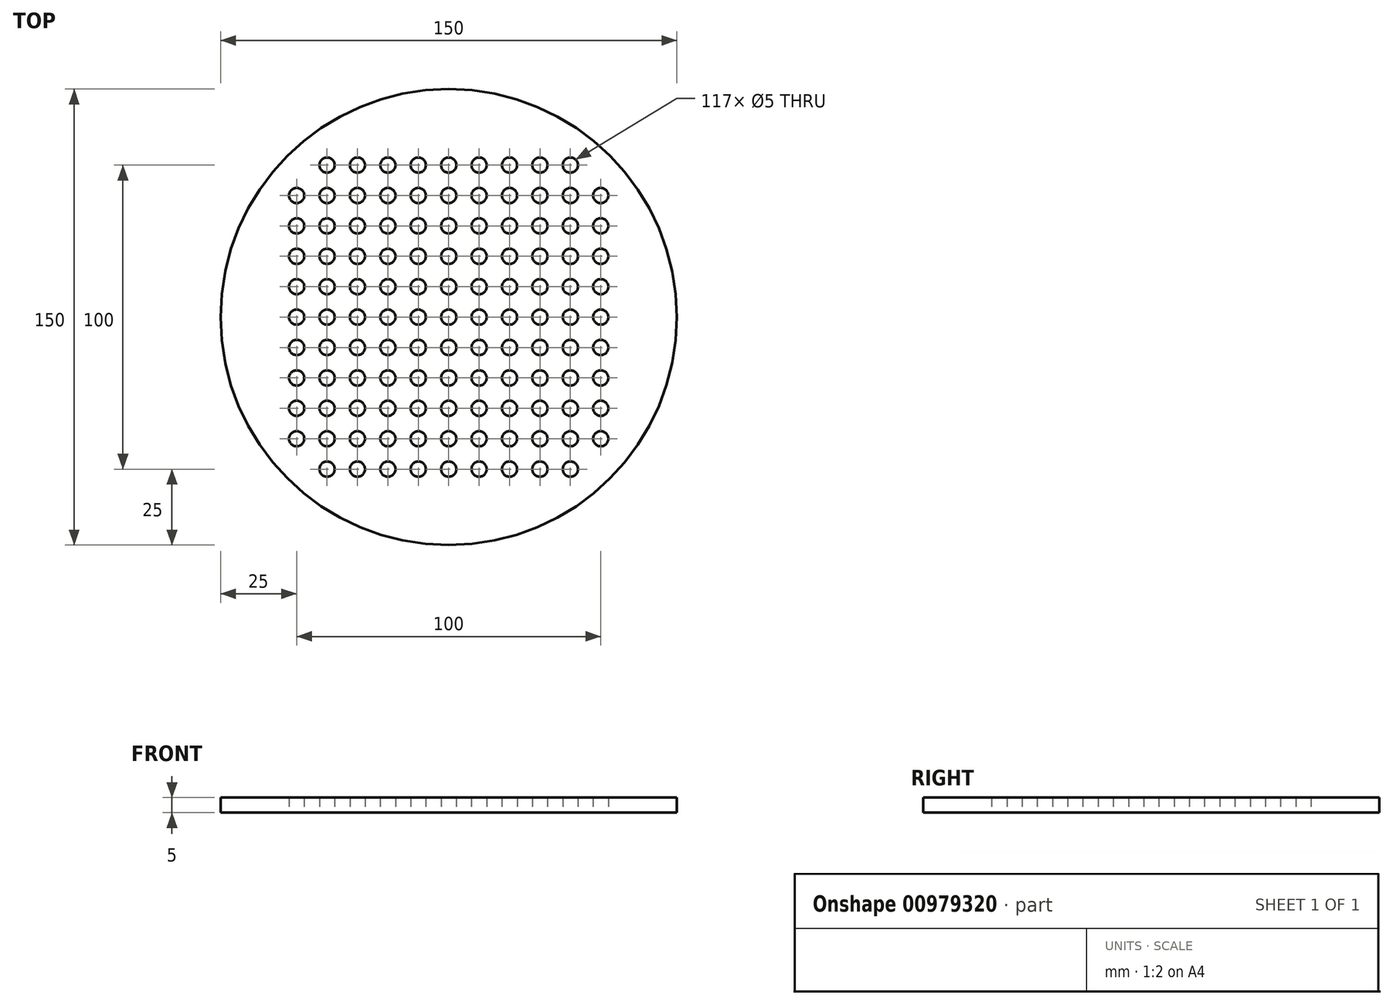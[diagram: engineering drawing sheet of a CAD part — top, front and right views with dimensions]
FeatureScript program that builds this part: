
annotation { "Feature Type Name" : "Feature", "Feature Type Description" : "" }
export const myFeature = defineFeature(function(context is Context, id is Id, definition is map)
    precondition{}
    {
        {
            var Q0;
            Q0=qCreatedBy(makeId("Top.planeOp"),FACE);
            var sketch = newSketch(context, id + "F0", { "sketchPlane" : qUnion([Q0])});
            skCircle(sketch, "E0", {"center": v(0, 0) * mm, "radius": 75 * mm});
            skCircle(sketch, "E1", {"center": v(0, 0) * mm, "radius": 2.5 * mm});
            skCircle(sketch, "E2.0.1.0", {"center": v(0, 10) * mm, "radius": 2.5 * mm});
            skCircle(sketch, "E2.0.2.0", {"center": v(0, 20) * mm, "radius": 2.5 * mm});
            skCircle(sketch, "E2.0.3.0", {"center": v(0, 30) * mm, "radius": 2.5 * mm});
            skCircle(sketch, "E2.0.4.0", {"center": v(0, 40) * mm, "radius": 2.5 * mm});
            skCircle(sketch, "E2.0.5.0", {"center": v(0, 50) * mm, "radius": 2.5 * mm});
            skCircle(sketch, "E2.1.0.0", {"center": v(10, 0) * mm, "radius": 2.5 * mm});
            skCircle(sketch, "E2.1.1.0", {"center": v(10, 10) * mm, "radius": 2.5 * mm});
            skCircle(sketch, "E2.1.2.0", {"center": v(10, 20) * mm, "radius": 2.5 * mm});
            skCircle(sketch, "E2.1.3.0", {"center": v(10, 30) * mm, "radius": 2.5 * mm});
            skCircle(sketch, "E2.1.4.0", {"center": v(10, 40) * mm, "radius": 2.5 * mm});
            skCircle(sketch, "E2.1.5.0", {"center": v(10, 50) * mm, "radius": 2.5 * mm});
            skCircle(sketch, "E2.2.0.0", {"center": v(20, 0) * mm, "radius": 2.5 * mm});
            skCircle(sketch, "E2.2.1.0", {"center": v(20, 10) * mm, "radius": 2.5 * mm});
            skCircle(sketch, "E2.2.2.0", {"center": v(20, 20) * mm, "radius": 2.5 * mm});
            skCircle(sketch, "E2.2.3.0", {"center": v(20, 30) * mm, "radius": 2.5 * mm});
            skCircle(sketch, "E2.2.4.0", {"center": v(20, 40) * mm, "radius": 2.5 * mm});
            skCircle(sketch, "E2.2.5.0", {"center": v(20, 50) * mm, "radius": 2.5 * mm});
            skCircle(sketch, "E2.3.0.0", {"center": v(30, 0) * mm, "radius": 2.5 * mm});
            skCircle(sketch, "E2.3.1.0", {"center": v(30, 10) * mm, "radius": 2.5 * mm});
            skCircle(sketch, "E2.3.2.0", {"center": v(30, 20) * mm, "radius": 2.5 * mm});
            skCircle(sketch, "E2.3.3.0", {"center": v(30, 30) * mm, "radius": 2.5 * mm});
            skCircle(sketch, "E2.3.4.0", {"center": v(30, 40) * mm, "radius": 2.5 * mm});
            skCircle(sketch, "E2.3.5.0", {"center": v(30, 50) * mm, "radius": 2.5 * mm});
            skCircle(sketch, "E2.4.0.0", {"center": v(40, 0) * mm, "radius": 2.5 * mm});
            skCircle(sketch, "E2.4.1.0", {"center": v(40, 10) * mm, "radius": 2.5 * mm});
            skCircle(sketch, "E2.4.2.0", {"center": v(40, 20) * mm, "radius": 2.5 * mm});
            skCircle(sketch, "E2.4.3.0", {"center": v(40, 30) * mm, "radius": 2.5 * mm});
            skCircle(sketch, "E2.4.4.0", {"center": v(40, 40) * mm, "radius": 2.5 * mm});
            skCircle(sketch, "E2.4.5.0", {"center": v(40, 50) * mm, "radius": 2.5 * mm});
            skCircle(sketch, "E2.5.0.0", {"center": v(50, 0) * mm, "radius": 2.5 * mm});
            skCircle(sketch, "E2.5.1.0", {"center": v(50, 10) * mm, "radius": 2.5 * mm});
            skCircle(sketch, "E2.5.2.0", {"center": v(50, 20) * mm, "radius": 2.5 * mm});
            skCircle(sketch, "E2.5.3.0", {"center": v(50, 30) * mm, "radius": 2.5 * mm});
            skCircle(sketch, "E2.5.4.0", {"center": v(50, 40) * mm, "radius": 2.5 * mm});
            skLineSegment(sketch, "E2.direction1", {"start": v(0, 0) * mm, "end": v(10, 0) * mm, "construction": true});
            skLineSegment(sketch, "E2.direction2", {"start": v(0, 0) * mm, "end": v(0, 10) * mm, "construction": true});
            skLineSegment(sketch, "E3", {"start": v(0, 83.12) * mm, "end": v(0, -89.64) * mm, "construction": true});
            skCircle(sketch, "E4.MirrorC", {"center": v(-20, 20) * mm, "radius": 2.5 * mm});
            skCircle(sketch, "E5.MirrorC", {"center": v(-10, 0) * mm, "radius": 2.5 * mm});
            skCircle(sketch, "E6.MirrorC", {"center": v(-10, 30) * mm, "radius": 2.5 * mm});
            skCircle(sketch, "E7.MirrorC", {"center": v(-50, 0) * mm, "radius": 2.5 * mm});
            skCircle(sketch, "E8.MirrorC", {"center": v(-20, 40) * mm, "radius": 2.5 * mm});
            skCircle(sketch, "E9.MirrorC", {"center": v(-40, 10) * mm, "radius": 2.5 * mm});
            skCircle(sketch, "E10.MirrorC", {"center": v(-10, 10) * mm, "radius": 2.5 * mm});
            skCircle(sketch, "E11.MirrorC", {"center": v(-20, 0) * mm, "radius": 2.5 * mm});
            skCircle(sketch, "E12.MirrorC", {"center": v(-30, 20) * mm, "radius": 2.5 * mm});
            skCircle(sketch, "E13.MirrorC", {"center": v(-10, 20) * mm, "radius": 2.5 * mm});
            skCircle(sketch, "E14.MirrorC", {"center": v(-20, 10) * mm, "radius": 2.5 * mm});
            skCircle(sketch, "E15.MirrorC", {"center": v(-50, 10) * mm, "radius": 2.5 * mm});
            skCircle(sketch, "E16.MirrorC", {"center": v(-30, 40) * mm, "radius": 2.5 * mm});
            skCircle(sketch, "E17.MirrorC", {"center": v(-40, 40) * mm, "radius": 2.5 * mm});
            skCircle(sketch, "E18.MirrorC", {"center": v(-10, 50) * mm, "radius": 2.5 * mm});
            skCircle(sketch, "E19.MirrorC", {"center": v(-50, 30) * mm, "radius": 2.5 * mm});
            skCircle(sketch, "E20.MirrorC", {"center": v(-40, 0) * mm, "radius": 2.5 * mm});
            skCircle(sketch, "E21.MirrorC", {"center": v(-30, 10) * mm, "radius": 2.5 * mm});
            skCircle(sketch, "E22.MirrorC", {"center": v(-30, 30) * mm, "radius": 2.5 * mm});
            skCircle(sketch, "E23.MirrorC", {"center": v(-20, 50) * mm, "radius": 2.5 * mm});
            skCircle(sketch, "E24.MirrorC", {"center": v(-30, 0) * mm, "radius": 2.5 * mm});
            skCircle(sketch, "E25.MirrorC", {"center": v(-40, 20) * mm, "radius": 2.5 * mm});
            skCircle(sketch, "E26.MirrorC", {"center": v(-40, 50) * mm, "radius": 2.5 * mm});
            skCircle(sketch, "E27.MirrorC", {"center": v(-10, 40) * mm, "radius": 2.5 * mm});
            skCircle(sketch, "E28.MirrorC", {"center": v(-50, 20) * mm, "radius": 2.5 * mm});
            skCircle(sketch, "E29.MirrorC", {"center": v(-30, 50) * mm, "radius": 2.5 * mm});
            skCircle(sketch, "E30.MirrorC", {"center": v(-40, 30) * mm, "radius": 2.5 * mm});
            skCircle(sketch, "E31.MirrorC", {"center": v(-50, 40) * mm, "radius": 2.5 * mm});
            skCircle(sketch, "E32.MirrorC", {"center": v(-20, 30) * mm, "radius": 2.5 * mm});
            skLineSegment(sketch, "E33", {"start": v(-88.16, 0) * mm, "end": v(90.2, 0) * mm, "construction": true});
            skCircle(sketch, "E34.MirrorC", {"center": v(0, -10) * mm, "radius": 2.5 * mm});
            skCircle(sketch, "E35.MirrorC", {"center": v(20, -20) * mm, "radius": 2.5 * mm});
            skCircle(sketch, "E36.MirrorC", {"center": v(-30, -50) * mm, "radius": 2.5 * mm});
            skCircle(sketch, "E37.MirrorC", {"center": v(-10, -30) * mm, "radius": 2.5 * mm});
            skCircle(sketch, "E38.MirrorC", {"center": v(20, -30) * mm, "radius": 2.5 * mm});
            skCircle(sketch, "E39.MirrorC", {"center": v(0, -20) * mm, "radius": 2.5 * mm});
            skCircle(sketch, "E40.MirrorC", {"center": v(20, -10) * mm, "radius": 2.5 * mm});
            skCircle(sketch, "E41.MirrorC", {"center": v(-50, -10) * mm, "radius": 2.5 * mm});
            skCircle(sketch, "E42.MirrorC", {"center": v(-20, -30) * mm, "radius": 2.5 * mm});
            skCircle(sketch, "E43.MirrorC", {"center": v(30, -20) * mm, "radius": 2.5 * mm});
            skCircle(sketch, "E44.MirrorC", {"center": v(-30, -30) * mm, "radius": 2.5 * mm});
            skCircle(sketch, "E45.MirrorC", {"center": v(40, -10) * mm, "radius": 2.5 * mm});
            skCircle(sketch, "E46.MirrorC", {"center": v(-10, -10) * mm, "radius": 2.5 * mm});
            skCircle(sketch, "E47.MirrorC", {"center": v(40, -20) * mm, "radius": 2.5 * mm});
            skCircle(sketch, "E48.MirrorC", {"center": v(-20, -20) * mm, "radius": 2.5 * mm});
            skCircle(sketch, "E49.MirrorC", {"center": v(-10, -50) * mm, "radius": 2.5 * mm});
            skCircle(sketch, "E50.MirrorC", {"center": v(-40, -30) * mm, "radius": 2.5 * mm});
            skCircle(sketch, "E51.MirrorC", {"center": v(40, -50) * mm, "radius": 2.5 * mm});
            skCircle(sketch, "E52.MirrorC", {"center": v(30, -40) * mm, "radius": 2.5 * mm});
            skCircle(sketch, "E53.MirrorC", {"center": v(10, -40) * mm, "radius": 2.5 * mm});
            skCircle(sketch, "E54.MirrorC", {"center": v(-50, -40) * mm, "radius": 2.5 * mm});
            skCircle(sketch, "E55.MirrorC", {"center": v(0, -30) * mm, "radius": 2.5 * mm});
            skCircle(sketch, "E56.MirrorC", {"center": v(-10, -40) * mm, "radius": 2.5 * mm});
            skCircle(sketch, "E57.MirrorC", {"center": v(30, -10) * mm, "radius": 2.5 * mm});
            skCircle(sketch, "E58.MirrorC", {"center": v(-30, -40) * mm, "radius": 2.5 * mm});
            skCircle(sketch, "E59.MirrorC", {"center": v(-20, -40) * mm, "radius": 2.5 * mm});
            skCircle(sketch, "E60.MirrorC", {"center": v(-20, -50) * mm, "radius": 2.5 * mm});
            skCircle(sketch, "E61.MirrorC", {"center": v(10, -30) * mm, "radius": 2.5 * mm});
            skCircle(sketch, "E62.MirrorC", {"center": v(10, -10) * mm, "radius": 2.5 * mm});
            skCircle(sketch, "E63.MirrorC", {"center": v(0, -50) * mm, "radius": 2.5 * mm});
            skCircle(sketch, "E64.MirrorC", {"center": v(40, -40) * mm, "radius": 2.5 * mm});
            skCircle(sketch, "E65.MirrorC", {"center": v(30, -50) * mm, "radius": 2.5 * mm});
            skCircle(sketch, "E66.MirrorC", {"center": v(10, -20) * mm, "radius": 2.5 * mm});
            skCircle(sketch, "E67.MirrorC", {"center": v(-40, -50) * mm, "radius": 2.5 * mm});
            skCircle(sketch, "E68.MirrorC", {"center": v(50, -40) * mm, "radius": 2.5 * mm});
            skCircle(sketch, "E69.MirrorC", {"center": v(50, -30) * mm, "radius": 2.5 * mm});
            skCircle(sketch, "E70.MirrorC", {"center": v(-40, -10) * mm, "radius": 2.5 * mm});
            skCircle(sketch, "E71.MirrorC", {"center": v(50, -20) * mm, "radius": 2.5 * mm});
            skCircle(sketch, "E72.MirrorC", {"center": v(-40, -40) * mm, "radius": 2.5 * mm});
            skCircle(sketch, "E73.MirrorC", {"center": v(50, -10) * mm, "radius": 2.5 * mm});
            skCircle(sketch, "E74.MirrorC", {"center": v(-30, -20) * mm, "radius": 2.5 * mm});
            skCircle(sketch, "E75.MirrorC", {"center": v(0, -40) * mm, "radius": 2.5 * mm});
            skCircle(sketch, "E76.MirrorC", {"center": v(20, -40) * mm, "radius": 2.5 * mm});
            skCircle(sketch, "E77.MirrorC", {"center": v(30, -30) * mm, "radius": 2.5 * mm});
            skCircle(sketch, "E78.MirrorC", {"center": v(-50, -30) * mm, "radius": 2.5 * mm});
            skCircle(sketch, "E79.MirrorC", {"center": v(-50, -20) * mm, "radius": 2.5 * mm});
            skCircle(sketch, "E80.MirrorC", {"center": v(20, -50) * mm, "radius": 2.5 * mm});
            skCircle(sketch, "E81.MirrorC", {"center": v(-10, -20) * mm, "radius": 2.5 * mm});
            skCircle(sketch, "E82.MirrorC", {"center": v(10, -50) * mm, "radius": 2.5 * mm});
            skCircle(sketch, "E83.MirrorC", {"center": v(-20, -10) * mm, "radius": 2.5 * mm});
            skCircle(sketch, "E84.MirrorC", {"center": v(40, -30) * mm, "radius": 2.5 * mm});
            skCircle(sketch, "E85.MirrorC", {"center": v(-30, -10) * mm, "radius": 2.5 * mm});
            skCircle(sketch, "E86.MirrorC", {"center": v(-40, -20) * mm, "radius": 2.5 * mm});
            skSolve(sketch);
        }
        {
            var Q0;
            Q0=makeQuery(id+"F0.imprint","IMPRINT",FACE,{"disambiguationData":[TD([[makeQuery(id+"F0.imprint","IMPRINT",EDGE,{"derivedFrom":sQuery(id+"F0.wireOp",EDGE,"E0")}),1.0]])]});
            extrude(context, id + "F1", {"entities" : qUnion([Q0]), "depth" : 5 * mm, "offsetDistance" : 25 * mm});
        }
    });
